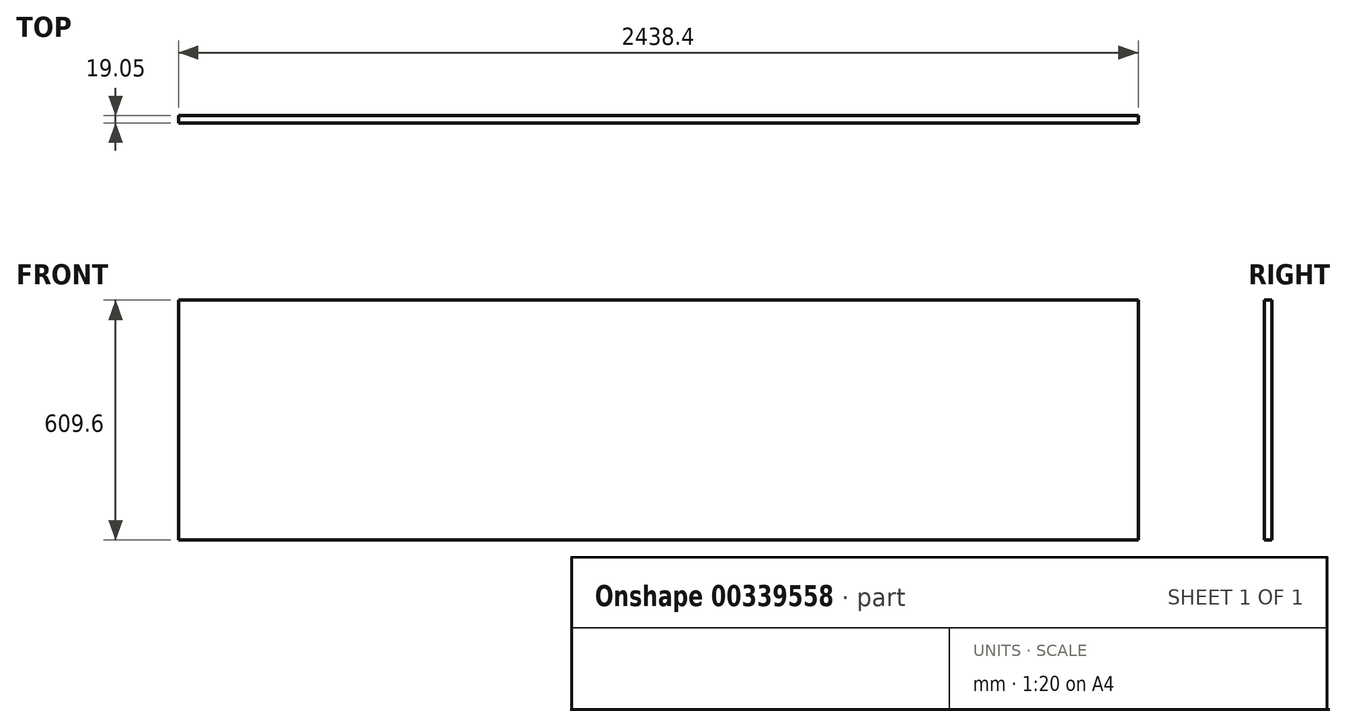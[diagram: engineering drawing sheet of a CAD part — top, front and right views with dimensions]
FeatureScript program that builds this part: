
annotation { "Feature Type Name" : "Feature", "Feature Type Description" : "" }
export const myFeature = defineFeature(function(context is Context, id is Id, definition is map)
    precondition{}
    {
        {
            var Q0;
            Q0=qCreatedBy(makeId("Front.planeOp"),FACE);
            var sketch = newSketch(context, id + "F0", { "sketchPlane" : qUnion([Q0])});
            skLineSegment(sketch, "E0.bottom", {"start": v(-51.31, 609.6) * mm, "end": v(2387.09, 609.6) * mm});
            skLineSegment(sketch, "E0.top", {"start": v(-51.31, 0) * mm, "end": v(2387.09, 0) * mm});
            skLineSegment(sketch, "E0.left", {"start": v(-51.31, 609.6) * mm, "end": v(-51.31, 0) * mm});
            skLineSegment(sketch, "E0.right", {"start": v(2387.09, 609.6) * mm, "end": v(2387.09, 0) * mm});
            skSolve(sketch);
        }
        {
            var Q0;
            Q0 = qSketchRegion(id + "F0", true);
            extrude(context, id + "F1", {"entities" : qUnion([Q0]), "depth" : 19.05 * mm});
        }
    });
